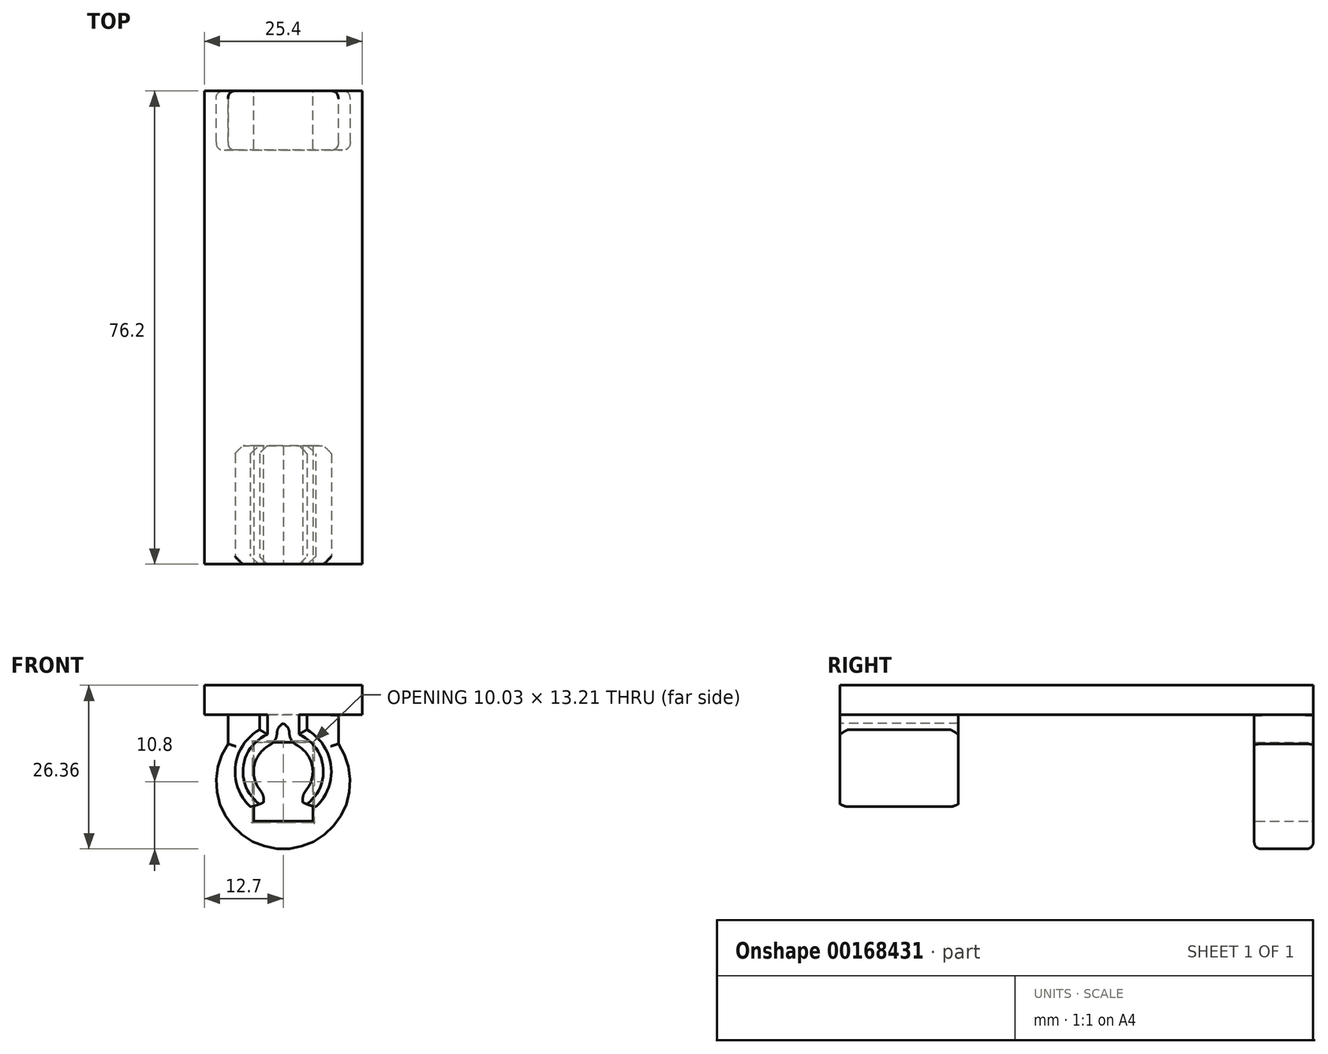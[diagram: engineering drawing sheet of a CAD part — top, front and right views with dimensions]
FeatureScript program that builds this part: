
annotation { "Feature Type Name" : "Feature", "Feature Type Description" : "" }
export const myFeature = defineFeature(function(context is Context, id is Id, definition is map)
    precondition{}
    {
        {
            var Q0;
            Q0=qCreatedBy(makeId("Front.planeOp"),FACE);
            var sketch = newSketch(context, id + "F0", { "sketchPlane" : qUnion([Q0])});
            skCircle(sketch, "E0", {"center": v(0, 0) * mm, "radius": 10.8 * mm});
            skPoint(sketch, "E1", {"position": v(0, 10.8) * mm});
            skLineSegment(sketch, "E2", {"start": v(0, 10.8) * mm, "end": v(8.89, 10.72) * mm});
            skLineSegment(sketch, "E3", {"start": v(0, 10.8) * mm, "end": v(-8.9, 10.8) * mm});
            skLineSegment(sketch, "E4", {"start": v(0, 10.8) * mm, "end": v(0, 3.5) * mm, "construction": true});
            skLineSegment(sketch, "E5.bottom", {"start": v(-4.76, 6.35) * mm, "end": v(4.76, 6.35) * mm});
            skLineSegment(sketch, "E5.top", {"start": v(-4.76, -6.35) * mm, "end": v(4.76, -6.35) * mm});
            skLineSegment(sketch, "E5.left", {"start": v(-4.76, 6.35) * mm, "end": v(-4.76, -6.35) * mm});
            skLineSegment(sketch, "E5.right", {"start": v(4.76, 6.35) * mm, "end": v(4.76, -6.35) * mm});
            skLineSegment(sketch, "E6", {"start": v(8.89, 10.72) * mm, "end": v(8.89, 6.12) * mm});
            skLineSegment(sketch, "E7", {"start": v(-8.9, 10.8) * mm, "end": v(-8.9, 6.12) * mm});
            skSolve(sketch);
        }
        {
            var Q0;
            {var subQ0=sQuery(id+"F0.wireOp",EDGE,"E0");var subQ1=makeQuery(id+"F0.imprint","INTERSECT",VERTEX,{"derivedFrom":[subQ0,sQuery(id+"F0.wireOp",EDGE,"uCNubuKe-HXJy-9hrr-weBs-rP70OjiO0xio")]});Q0=makeQuery(id+"F0.imprint","IMPRINT",FACE,{"disambiguationData":[TD([[makeQuery(id+"F0.imprint","IMPRINT",EDGE,{"disambiguationData":[TD([[subQ1,-1.0]])],"derivedFrom":subQ0}),1.0]])]});}
            var Q1;
            {var subQ0=sQuery(id+"F0.wireOp",EDGE,"E3");Q1=makeQuery(id+"F0.imprint","IMPRINT",FACE,{"disambiguationData":[TD([[makeQuery(id+"F0.imprint","IMPRINT",EDGE,{"derivedFrom":subQ0}),1.0]])]});}
            var Q2;
            {var subQ0=sQuery(id+"F0.wireOp",EDGE,"uCNubuKe-HXJy-9hrr-weBs-rP70OjiO0xio");Q2=makeQuery(id+"F0.imprint","IMPRINT",FACE,{"disambiguationData":[TD([[makeQuery(id+"F0.imprint","IMPRINT",EDGE,{"derivedFrom":subQ0}),-1.0]])]});}
            var Q3;
            {var subQ0=sQuery(id+"F0.wireOp",EDGE,"E6");Q3=makeQuery(id+"F0.imprint","IMPRINT",FACE,{"disambiguationData":[TD([[makeQuery(id+"F0.imprint","IMPRINT",EDGE,{"derivedFrom":subQ0}),-1.0]])]});}
            extrude(context, id + "F1", {"entities" : qUnion([Q0, Q1, Q2, Q3]), "depth" : 9.52 * mm});
        }
        {
            var Q0;
            Q0=makeQuery(id+"F1.opExtrude","CAP_EDGE",EDGE,{"disambiguationData":[OSD([sQuery(id+"F0.wireOp",EDGE,"E0")])],"isStart":false});
            var Q1;
            Q1=makeQuery(id+"F1.opExtrude","CAP_EDGE",EDGE,{"disambiguationData":[OSD([sQuery(id+"F0.wireOp",EDGE,"E0")])],"isStart":true});
            var Q2;
            Q2=makeQuery(id+"F1.opExtrude","CAP_EDGE",EDGE,{"disambiguationData":[OSD([sQuery(id+"F0.wireOp",EDGE,"uCNubuKe-HXJy-9hrr-weBs-rP70OjiO0xio")])],"isStart":false});
            var Q3;
            Q3=makeQuery(id+"F1.opExtrude","CAP_EDGE",EDGE,{"disambiguationData":[OSD([sQuery(id+"F0.wireOp",EDGE,"uCNubuKe-HXJy-9hrr-weBs-rP70OjiO0xio")])],"isStart":true});
            var Q4;
            Q4=makeQuery(id+"F1.opExtrude","CAP_EDGE",EDGE,{"disambiguationData":[OSD([sQuery(id+"F0.wireOp",EDGE,"koIsB0C4-fgXi-a8SS-ArQ9-EuaNeWwu5wdR")])],"isStart":false});
            var Q5;
            Q5=makeQuery(id+"F1.opExtrude","CAP_EDGE",EDGE,{"disambiguationData":[OSD([sQuery(id+"F0.wireOp",EDGE,"koIsB0C4-fgXi-a8SS-ArQ9-EuaNeWwu5wdR")])],"isStart":true});
            var Q6;
            Q6=makeQuery(id+"F1.opExtrude","CAP_EDGE",EDGE,{"disambiguationData":[OSD([sQuery(id+"F0.wireOp",EDGE,"E6")])],"isStart":true});
            var Q7;
            Q7=makeQuery(id+"F1.opExtrude","CAP_EDGE",EDGE,{"disambiguationData":[OSD([sQuery(id+"F0.wireOp",EDGE,"E6")])],"isStart":false});
            var Q8;
            Q8=makeQuery(id+"F1.opExtrude","CAP_EDGE",EDGE,{"disambiguationData":[OSD([sQuery(id+"F0.wireOp",EDGE,"E7")])],"isStart":true});
            var Q9;
            Q9=makeQuery(id+"F1.opExtrude","CAP_EDGE",EDGE,{"disambiguationData":[OSD([sQuery(id+"F0.wireOp",EDGE,"E7")])],"isStart":false});
            fillet(context, id + "F2", {"entities" : qUnion([Q0, Q1, Q2, Q3, Q4, Q5, Q6, Q7, Q8, Q9]), "radius" : 1.27 * mm, "tangentPropagation" : true, "rho" : .5, "crossSection" : FilletCrossSection.CONIC, "allowEdgeOverflow" : false});
        }
        {
            var Q0;
            Q0=makeQuery(id+"F1.opExtrude","CAP_EDGE",EDGE,{"disambiguationData":[OSD([sQuery(id+"F0.wireOp",EDGE,"E5.right")])],"isStart":false});
            var Q1;
            Q1=makeQuery(id+"F1.opExtrude","CAP_EDGE",EDGE,{"disambiguationData":[OSD([sQuery(id+"F0.wireOp",EDGE,"E5.right")])],"isStart":true});
            var Q2;
            Q2=makeQuery(id+"F1.opExtrude","CAP_EDGE",EDGE,{"disambiguationData":[OSD([sQuery(id+"F0.wireOp",EDGE,"E5.left")])],"isStart":false});
            var Q3;
            Q3=makeQuery(id+"F1.opExtrude","CAP_EDGE",EDGE,{"disambiguationData":[OSD([sQuery(id+"F0.wireOp",EDGE,"E5.left")])],"isStart":true});
            var Q4;
            Q4=makeQuery(id+"F1.opExtrude","CAP_EDGE",EDGE,{"disambiguationData":[OSD([sQuery(id+"F0.wireOp",EDGE,"E5.top")])],"isStart":true});
            var Q5;
            Q5=makeQuery(id+"F1.opExtrude","CAP_EDGE",EDGE,{"disambiguationData":[OSD([sQuery(id+"F0.wireOp",EDGE,"E5.bottom")])],"isStart":true});
            var Q6;
            Q6=makeQuery(id+"F1.opExtrude","CAP_EDGE",EDGE,{"disambiguationData":[OSD([sQuery(id+"F0.wireOp",EDGE,"E5.bottom")])],"isStart":false});
            var Q7;
            Q7=makeQuery(id+"F1.opExtrude","CAP_EDGE",EDGE,{"disambiguationData":[OSD([sQuery(id+"F0.wireOp",EDGE,"E5.top")])],"isStart":false});
            fillet(context, id + "F3", {"entities" : qUnion([Q0, Q1, Q2, Q3, Q4, Q5, Q6, Q7]), "radius" : 0.25 * mm, "tangentPropagation" : true, "rho" : .9, "crossSection" : FilletCrossSection.CONIC, "allowEdgeOverflow" : false});
        }
        {
            var Q0;
            Q0=qCreatedBy(makeId("Front.planeOp"),FACE);
            var sketch = newSketch(context, id + "F4", { "sketchPlane" : qUnion([Q0])});
            skLineSegment(sketch, "E8", {"start": v(0, 10.8) * mm, "end": v(0, 13.18) * mm, "construction": true});
            skLineSegment(sketch, "E9.bottom", {"start": v(-12.7, 15.56) * mm, "end": v(12.7, 15.56) * mm});
            skLineSegment(sketch, "E9.top", {"start": v(-12.7, 10.8) * mm, "end": v(12.7, 10.8) * mm});
            skLineSegment(sketch, "E9.left", {"start": v(-12.7, 15.56) * mm, "end": v(-12.7, 10.8) * mm});
            skLineSegment(sketch, "E9.right", {"start": v(12.7, 15.56) * mm, "end": v(12.7, 10.8) * mm});
            skPoint(sketch, "E9.middle", {"position": v(0, 13.18) * mm});
            skSolve(sketch);
        }
        {
            var Q0;
            Q0=makeQuery(id+"F4.imprint","IMPRINT",FACE,{"disambiguationData":[TD([[makeQuery(id+"F4.imprint","IMPRINT",EDGE,{"derivedFrom":sQuery(id+"F4.wireOp",EDGE,"E9.bottom")}),-1.0]])]});
            extrude(context, id + "F5", {"entities" : qUnion([Q0]), "operationType" : NewBodyOperationType.ADD, "depth" : 76.2 * mm});
        }
        {
            var Q0;
            Q0=qCreatedBy(makeId("Front.planeOp"),FACE);
            cPlane(context, id + "F6", {"entities" : qUnion([Q0]), "cplaneType" : CPlaneType.OFFSET, "offset" : 76.2 * mm, "width" : 152.4 * mm, "height" : 152.4 * mm});
        }
        {
            var Q0;
            Q0=qCreatedBy(id+"F6.planeOp",FACE);
            var sketch = newSketch(context, id + "F7", { "sketchPlane" : qUnion([Q0])});
            skPoint(sketch, "E10", {"position": v(0, 0) * mm});
            skCircle(sketch, "E11", {"center": v(0, 1.66) * mm, "radius": 4.76 * mm});
            skLineSegment(sketch, "E12", {"start": v(0, 10.8) * mm, "end": v(0, 6.43) * mm});
            skLineSegment(sketch, "E13", {"start": v(0, -3.1) * mm, "end": v(0, -6.08) * mm});
            skLineSegment(sketch, "E14", {"start": v(0, 1.66) * mm, "end": v(2.86, 1.66) * mm, "construction": true});
            skLineSegment(sketch, "E15", {"start": v(2.86, 1.66) * mm, "end": v(2.86, -2.15) * mm, "construction": true});
            skLineSegment(sketch, "E16", {"start": v(0, 10.8) * mm, "end": v(3.81, 10.8) * mm});
            skLineSegment(sketch, "E17", {"start": v(0, 10.8) * mm, "end": v(0, 10.8) * mm});
            skCircle(sketch, "E18", {"center": v(0, 1.66) * mm, "radius": 7.75 * mm});
            skLineSegment(sketch, "E19", {"start": v(2.86, 1.66) * mm, "end": v(3.65, 1.66) * mm, "construction": true});
            skLineSegment(sketch, "E20", {"start": v(3.65, 1.66) * mm, "end": v(3.65, -5.17) * mm, "construction": true});
            skLineSegment(sketch, "E21", {"start": v(2.86, -2.15) * mm, "end": v(3.65, -5.17) * mm});
            skLineSegment(sketch, "E22", {"start": v(3.81, 10.8) * mm, "end": v(3.81, 8.4) * mm});
            skFitSpline(sketch, "E23", {"points": [v(0, 9.41) * mm, v(1.18, 6.28) * mm], "startDerivative": vector(4.42, -2.54) * mm, "endDerivative": vector(1.4, -4.22) * mm});
            skSolve(sketch);
        }
        {
            var Q0;
            {var subQ0=sQuery(id+"F7.wireOp",EDGE,"E16");Q0=makeQuery(id+"F7.imprint","IMPRINT",FACE,{"disambiguationData":[TD([[makeQuery(id+"F7.imprint","IMPRINT",EDGE,{"derivedFrom":subQ0}),-1.0]])]});}
            var Q1;
            {var subQ0=sQuery(id+"F7.wireOp",EDGE,"E21");Q1=makeQuery(id+"F7.imprint","IMPRINT",FACE,{"disambiguationData":[TD([[makeQuery(id+"F7.imprint","IMPRINT",EDGE,{"derivedFrom":subQ0}),1.0]])]});}
            extrude(context, id + "F8", {"entities" : qUnion([Q0, Q1]), "operationType" : NewBodyOperationType.ADD, "oppositeDirection" : true, "depth" : 19.05 * mm});
        }
        {
            var Q0;
            Q0=makeQuery(id+"F1.opExtrude","SWEPT_BODY",BODY,{"disambiguationData":[OSD([sQuery(id+"F0.wireOp",EDGE,"E0"),sQuery(id+"F0.wireOp",EDGE,"E2"),sQuery(id+"F0.wireOp",EDGE,"E3"),sQuery(id+"F0.wireOp",EDGE,"E5.bottom"),sQuery(id+"F0.wireOp",EDGE,"E5.top"),sQuery(id+"F0.wireOp",EDGE,"E5.left"),sQuery(id+"F0.wireOp",EDGE,"E5.right"),sQuery(id+"F0.wireOp",EDGE,"E6"),sQuery(id+"F0.wireOp",EDGE,"E7")])]});
            var Q1;
            Q1=qCreatedBy(makeId("Right.planeOp"),FACE);
            mirror(context, id + "F9", {"operationType" : NewBodyOperationType.ADD, "entities" : qUnion([Q0]), "mirrorPlane" : qUnion([Q1])});
        }
        {
            var Q0;
            Q0=makeQuery(id+"F9.opPattern","COPY",EDGE,{"derivedFrom":makeQuery(id+"F8.opExtrude","CAP_EDGE",EDGE,{"disambiguationData":[OSD([sQuery(id+"F7.wireOp",EDGE,"589a90df-d768-4e65-9d57-18af15b25602")])],"isStart":true}),"instanceName":"1"});
            var Q1;
            Q1=makeQuery(id+"F9.opPattern","COPY",EDGE,{"derivedFrom":makeQuery(id+"F8.opExtrude","CAP_EDGE",EDGE,{"disambiguationData":[OSD([sQuery(id+"F7.wireOp",EDGE,"589a90df-d768-4e65-9d57-18af15b25602")])],"isStart":false}),"instanceName":"1"});
            var Q2;
            Q2=makeQuery(id+"F8.opExtrude","CAP_EDGE",EDGE,{"disambiguationData":[OSD([sQuery(id+"F7.wireOp",EDGE,"589a90df-d768-4e65-9d57-18af15b25602")])],"isStart":true});
            var Q3;
            Q3=makeQuery(id+"F8.opExtrude","CAP_EDGE",EDGE,{"disambiguationData":[OSD([sQuery(id+"F7.wireOp",EDGE,"589a90df-d768-4e65-9d57-18af15b25602")])],"isStart":false});
            var Q4;
            Q4=makeQuery(id+"F9.opPattern","COPY",EDGE,{"derivedFrom":makeQuery(id+"F8.opExtrude","CAP_EDGE",EDGE,{"disambiguationData":[OSD([sQuery(id+"F7.wireOp",EDGE,"d686bfed-ccd7-4b10-82b9-1a6fa3bd24de")])],"isStart":true}),"instanceName":"1"});
            var Q5;
            Q5=makeQuery(id+"F8.opExtrude","CAP_EDGE",EDGE,{"disambiguationData":[OSD([sQuery(id+"F7.wireOp",EDGE,"d686bfed-ccd7-4b10-82b9-1a6fa3bd24de")])],"isStart":true});
            var Q6;
            Q6=makeQuery(id+"F9.opPattern","COPY",EDGE,{"derivedFrom":makeQuery(id+"F8.opExtrude","CAP_EDGE",EDGE,{"disambiguationData":[OSD([sQuery(id+"F7.wireOp",EDGE,"d686bfed-ccd7-4b10-82b9-1a6fa3bd24de")])],"isStart":false}),"instanceName":"1"});
            var Q7;
            Q7=makeQuery(id+"F8.opExtrude","CAP_EDGE",EDGE,{"disambiguationData":[OSD([sQuery(id+"F7.wireOp",EDGE,"d686bfed-ccd7-4b10-82b9-1a6fa3bd24de")])],"isStart":false});
            var Q8;
            Q8=makeQuery(id+"F9.opPattern","COPY",EDGE,{"derivedFrom":makeQuery(id+"F8.opExtrude","SWEPT_EDGE",EDGE,{"disambiguationData":[OSD([sQuery(id+"F7.wireOp",EDGE,"E11"),sQuery(id+"F7.wireOp",EDGE,"2310f6c3-1c6d-4b50-8885-317f6d58f5a4")])]}),"instanceName":"1"});
            var Q9;
            Q9=makeQuery(id+"F8.opExtrude","SWEPT_EDGE",EDGE,{"disambiguationData":[OSD([sQuery(id+"F7.wireOp",EDGE,"E11"),sQuery(id+"F7.wireOp",EDGE,"2310f6c3-1c6d-4b50-8885-317f6d58f5a4")])]});
            fillet(context, id + "F10", {"entities" : qUnion([Q0, Q1, Q2, Q3, Q4, Q5, Q6, Q7, Q8, Q9]), "radius" : 2.54 * mm, "tangentPropagation" : true, "rho" : 0.5, "crossSection" : FilletCrossSection.CONIC, "allowEdgeOverflow" : false});
        }
        {
            var Q0;
            Q0=makeQuery(id+"F9.opPattern","COPY",EDGE,{"derivedFrom":makeQuery(id+"F8.opExtrude","CAP_EDGE",EDGE,{"disambiguationData":[OSD([sQuery(id+"F7.wireOp",EDGE,"E18")])],"isStart":true}),"instanceName":"1"});
            var Q1;
            Q1=makeQuery(id+"F8.opExtrude","CAP_EDGE",EDGE,{"disambiguationData":[OSD([sQuery(id+"F7.wireOp",EDGE,"E18")])],"isStart":true});
            var Q2;
            Q2=makeQuery(id+"F8.opExtrude","CAP_EDGE",EDGE,{"disambiguationData":[OSD([sQuery(id+"F7.wireOp",EDGE,"E22")])],"isStart":true});
            var Q3;
            Q3=makeQuery(id+"F9.opPattern","COPY",EDGE,{"derivedFrom":makeQuery(id+"F8.opExtrude","CAP_EDGE",EDGE,{"disambiguationData":[OSD([sQuery(id+"F7.wireOp",EDGE,"E22")])],"isStart":true}),"instanceName":"1"});
            var Q4;
            Q4=makeQuery(id+"F8.opExtrude","CAP_EDGE",EDGE,{"disambiguationData":[OSD([sQuery(id+"F7.wireOp",EDGE,"E18")])],"isStart":false});
            var Q5;
            Q5=makeQuery(id+"F8.opExtrude","CAP_EDGE",EDGE,{"disambiguationData":[OSD([sQuery(id+"F7.wireOp",EDGE,"E22")])],"isStart":false});
            var Q6;
            Q6=makeQuery(id+"F9.opPattern","COPY",EDGE,{"derivedFrom":makeQuery(id+"F8.opExtrude","CAP_EDGE",EDGE,{"disambiguationData":[OSD([sQuery(id+"F7.wireOp",EDGE,"E18")])],"isStart":false}),"instanceName":"1"});
            var Q7;
            Q7=makeQuery(id+"F9.opPattern","COPY",EDGE,{"derivedFrom":makeQuery(id+"F8.opExtrude","CAP_EDGE",EDGE,{"disambiguationData":[OSD([sQuery(id+"F7.wireOp",EDGE,"E22")])],"isStart":false}),"instanceName":"1"});
            var Q8;
            Q8=makeQuery(id+"F9.opPattern","COPY",EDGE,{"derivedFrom":makeQuery(id+"F8.opExtrude","SWEPT_EDGE",EDGE,{"disambiguationData":[OSD([sQuery(id+"F7.wireOp",EDGE,"E18"),sQuery(id+"F7.wireOp",EDGE,"E21")])]}),"instanceName":"1"});
            var Q9;
            Q9=makeQuery(id+"F8.opExtrude","SWEPT_EDGE",EDGE,{"disambiguationData":[OSD([sQuery(id+"F7.wireOp",EDGE,"E18"),sQuery(id+"F7.wireOp",EDGE,"E21")])]});
            fillet(context, id + "F11", {"entities" : qUnion([Q0, Q1, Q2, Q3, Q4, Q5, Q6, Q7, Q8, Q9]), "radius" : 1.27 * mm, "tangentPropagation" : true, "rho" : 0.05, "crossSection" : FilletCrossSection.CONIC, "allowEdgeOverflow" : false});
        }
    });
